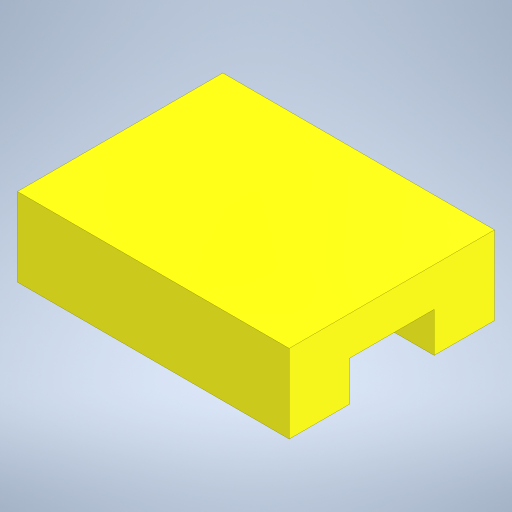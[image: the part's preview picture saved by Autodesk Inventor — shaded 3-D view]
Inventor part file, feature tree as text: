
AUTODESK INVENTOR PART (.ipt)
format: ipt  version: 2024 (Build 280153000, 153)  size: 196,096 bytes
history: native  units: mm
features: extrude x1, sketch x1
ambient origin geometry x8: Origin, YZ Plane, XZ Plane, XY Plane, X Axis, Y Axis, Z Axis, Center Point
bodies: Solid1 (feature_tree)
feature tree (2):
  extrude  "Extrusion1"  Depth=3.3mm
  sketch  "Sketch1"  dims[d0=17.0mm d1=3.3mm d2=6.5mm d3=5.0mm d4=7.0mm d5=22.5mm d6=0.0mm]
